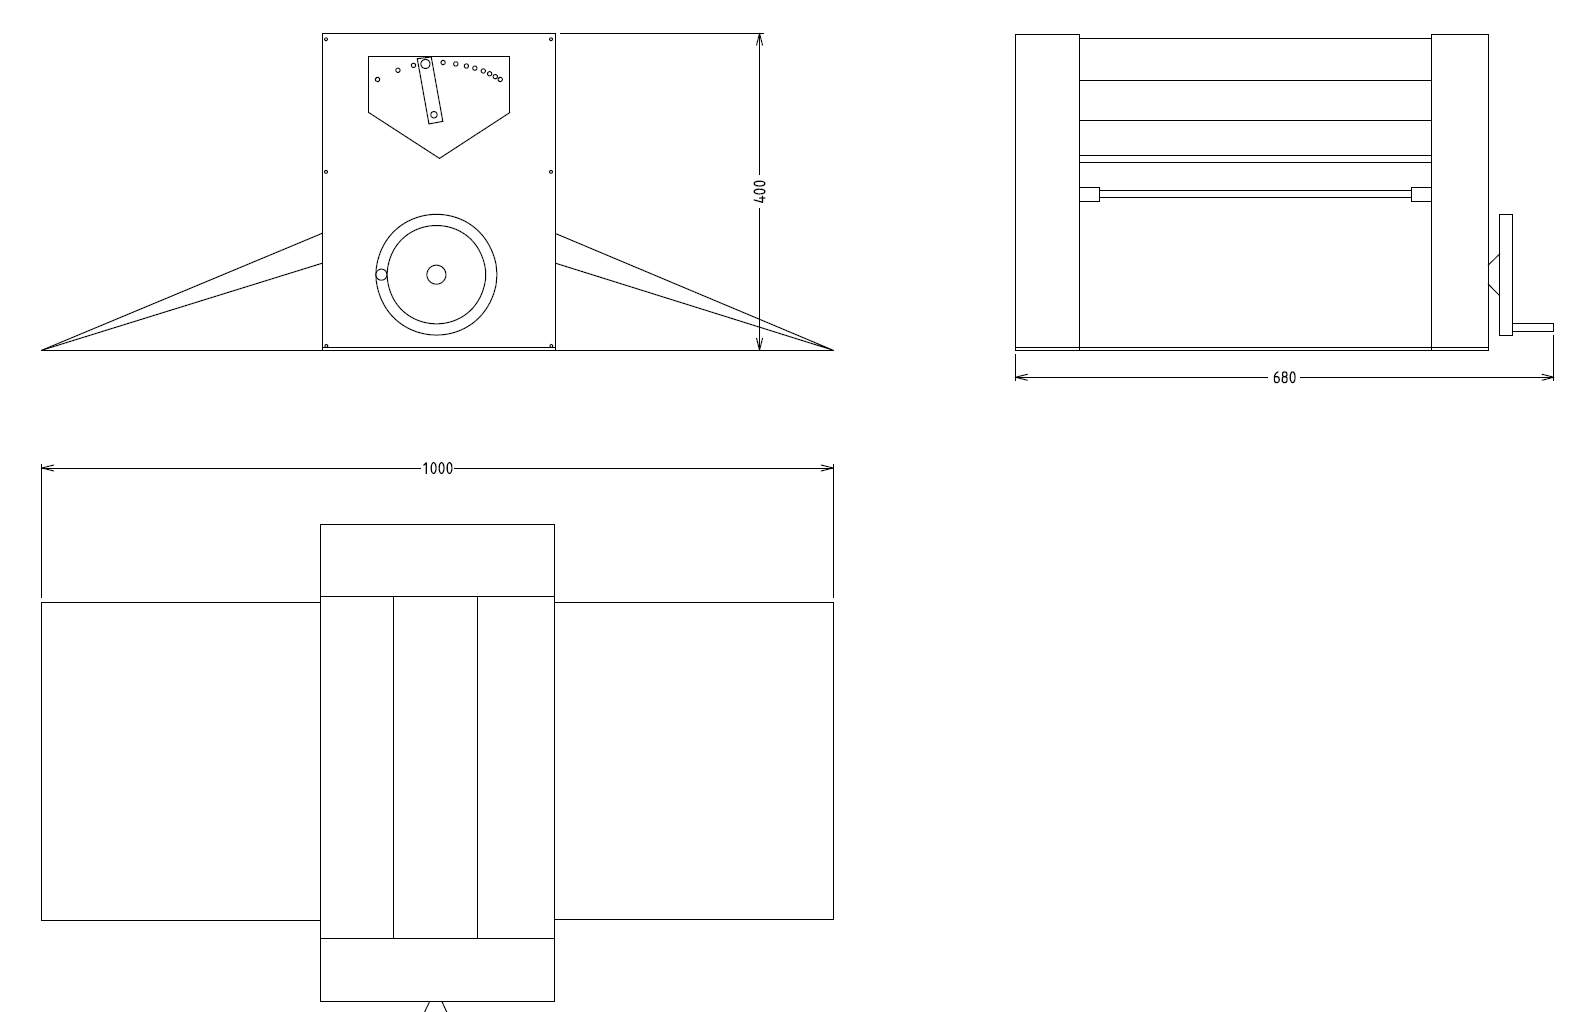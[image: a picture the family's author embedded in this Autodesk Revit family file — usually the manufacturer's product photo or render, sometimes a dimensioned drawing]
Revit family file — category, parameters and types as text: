
# Revit family: QF_ELECTROLUXPROFESSIONAL_603531_LMP400
name_source: partatom
category: Specialty Equipment
revit_build: Autodesk Revit 2018 (Build: 20190510_1515(x64)
units: mm (PartAtom-declared; Revit-internal decimal feet)

## family parameters
Always vertical = Yes
Cut with Voids When Loaded = No
Part Type = Normal
Room Calculation Point = No
Round Connector Dimension = Use Diameter
Shared = No
Work Plane-Based = No

## types (1)
- QF_ELECTROLUX_603531_LMP400
    Accessory = Yes
    Cold Water Size = 0 mm
    Compressed Air Pressure = 0.0 Pa
    Compressed Air Size = 0 mm
    Compressed Air Volume = 0.0 L/s
    Condensate Return Size = 0 mm
    Cycle = 0 Hz
    Depth Actual = 680 mm  [stored 2.23097 ft]
    Description = HAND DOUGH SHEETER-REMOV.S/S FLAPS-400MM
    Direct Waste Size = 0 mm
    Gas Input Pressure = 0
    Gas KW = 0
    Gas Size = 0 mm
    HP = 0 HP
    Height Actual = 400 mm  [stored 1.31234 ft]
    Hot Water Size = 0 mm
    Item Number = 603531
    Length Actual = 1000 mm  [stored 3.28084 ft]
    Manufacturer = Electrolux
    Model = LMP400
    Phase = 0
    Refrigerant Compressor Remote = Yes
    Refrigeration Liquid Line Size = 0 mm
    Refrigeration Suction Line Size = 0 mm
    Steam Pounds per Hour = 0
    Steam Supply Maximum Pressure = 0.0 Pa
    Steam Supply Minimum Pressure = 0.0 Pa
    Steam Supply Size = 0 mm
    URL = http://professional.electrolux.com
    URL Manufacturer = http://professional.electrolux.com
    Volts = 0 V
    Watts = 0 W
    Weight = 35.00 kg

note: source unit labels omitted for Gas Input Pressure — the stored unit's dimension contradicts the parameter name (converter mislabeling)

note: [stored X ft] marks values corroborated as IEEE doubles in the binary element streams (Revit-internal decimal feet)

## geometry (parser evidence)
native form markers: Sweep x4
no freeform markers — native parametric forms only
